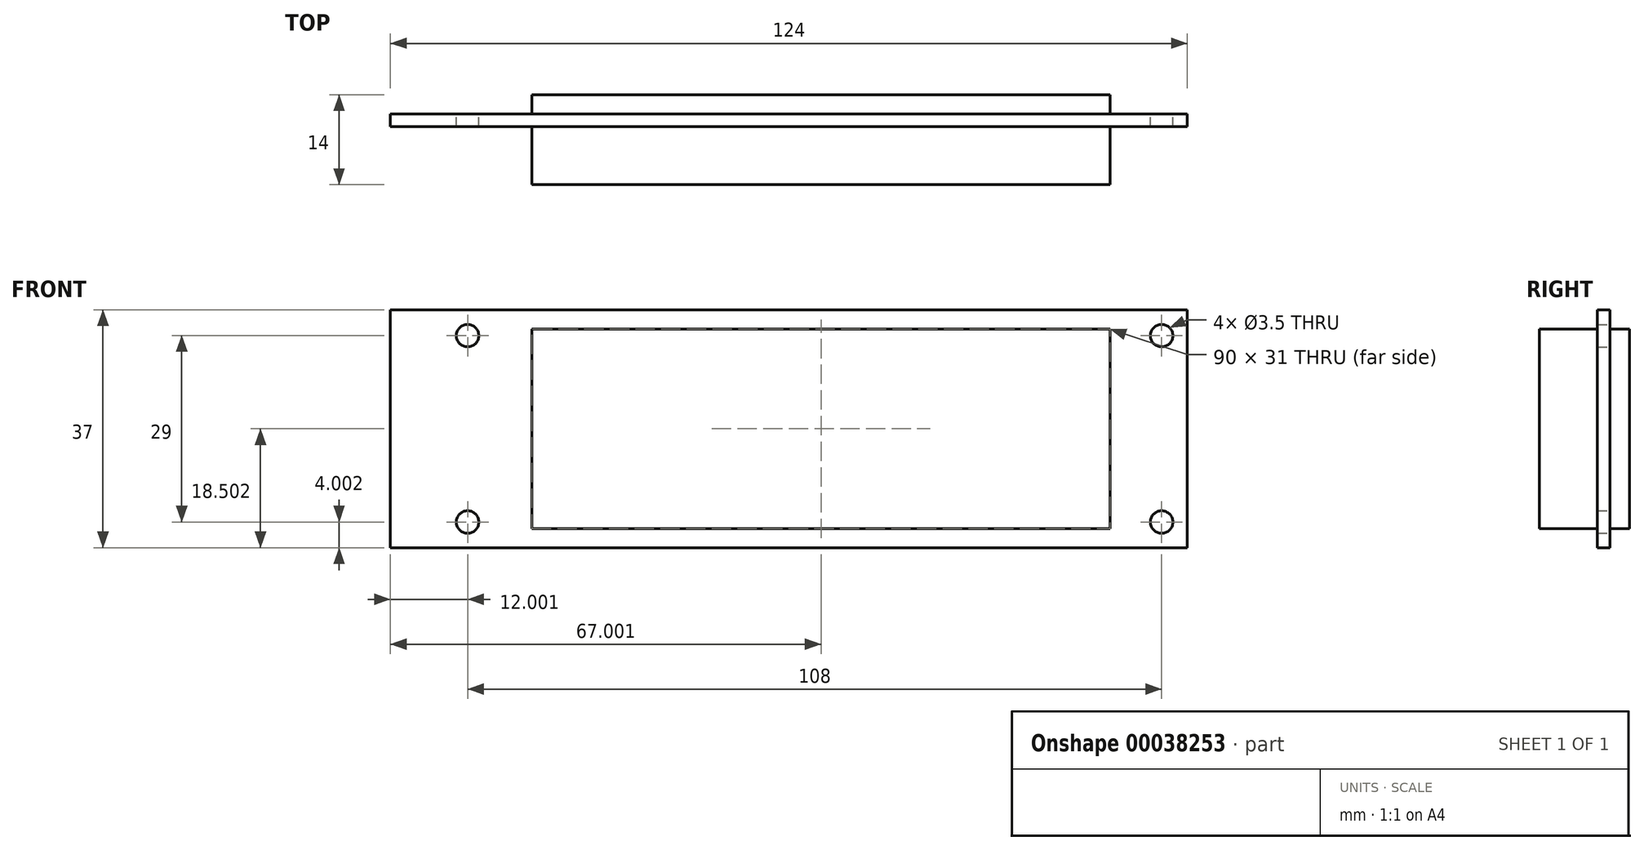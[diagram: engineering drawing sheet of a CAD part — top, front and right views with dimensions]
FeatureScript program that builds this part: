
annotation { "Feature Type Name" : "Feature", "Feature Type Description" : "" }
export const myFeature = defineFeature(function(context is Context, id is Id, definition is map)
    precondition{}
    {
        {
            var Q0;
            Q0=qCreatedBy(makeId("Front.planeOp"),FACE);
            var sketch = newSketch(context, id + "F0", { "sketchPlane" : qUnion([Q0])});
            skLineSegment(sketch, "E0.bottom", {"start": v(-121.3, -70.97) * mm, "end": v(2.7, -70.97) * mm});
            skLineSegment(sketch, "E0.top", {"start": v(-121.3, -33.97) * mm, "end": v(2.7, -33.97) * mm});
            skLineSegment(sketch, "E0.left", {"start": v(-121.3, -70.97) * mm, "end": v(-121.3, -33.97) * mm});
            skLineSegment(sketch, "E0.right", {"start": v(2.7, -70.97) * mm, "end": v(2.7, -33.97) * mm});
            skLineSegment(sketch, "E1.bottom", {"start": v(-99.3, -67.97) * mm, "end": v(-9.3, -67.97) * mm});
            skLineSegment(sketch, "E1.top", {"start": v(-99.3, -36.97) * mm, "end": v(-9.3, -36.97) * mm});
            skLineSegment(sketch, "E1.left", {"start": v(-99.3, -67.97) * mm, "end": v(-99.3, -36.97) * mm});
            skLineSegment(sketch, "E1.right", {"start": v(-9.3, -67.97) * mm, "end": v(-9.3, -36.97) * mm});
            skLineSegment(sketch, "E2", {"start": v(-109.3, -23.5) * mm, "end": v(-109.3, -79.6) * mm});
            skLineSegment(sketch, "E3", {"start": v(-131.68, -37.97) * mm, "end": v(-109.3, -37.97) * mm});
            skLineSegment(sketch, "E4", {"start": v(-135.53, -66.97) * mm, "end": v(-109.3, -66.97) * mm});
            skLineSegment(sketch, "E5", {"start": v(-1.3, -26.38) * mm, "end": v(-1.3, -82.28) * mm});
            skPoint(sketch, "E6", {"position": v(-109.3, -37.97) * mm});
            skPoint(sketch, "E7", {"position": v(-109.3, -66.97) * mm});
            skPoint(sketch, "E8", {"position": v(-1.3, -37.97) * mm});
            skPoint(sketch, "E9", {"position": v(-1.3, -66.97) * mm});
            skLineSegment(sketch, "E10.trimOffspring", {"start": v(-1.3, -37.97) * mm, "end": v(8.28, -37.97) * mm});
            skLineSegment(sketch, "E11.trimOffspring", {"start": v(-1.3, -66.97) * mm, "end": v(17.4, -66.97) * mm});
            skSolve(sketch);
        }
        {
            var Q0;
            {var subQ1=sQuery(id+"F0.wireOp",EDGE,"E4");var subQ5=sQuery(id+"F0.wireOp",EDGE,"E0.left");var subQ6=makeQuery(id+"F0.imprint","INTERSECT",VERTEX,{"derivedFrom":[subQ5,subQ1]});Q0=makeQuery(id+"F0.imprint","IMPRINT",FACE,{"disambiguationData":[TD([[makeQuery(id+"F0.imprint","IMPRINT",EDGE,{"disambiguationData":[TD([[subQ6,-1.0]])],"derivedFrom":subQ5}),-1.0]])]});}
            var Q1;
            {var subQ1=sQuery(id+"F0.wireOp",EDGE,"E0.left");var subQ5=sQuery(id+"F0.wireOp",EDGE,"E0.top");var subQ6=makeQuery(id+"F0.imprint","INTERSECT",VERTEX,{"derivedFrom":[subQ5,subQ1]});Q1=makeQuery(id+"F0.imprint","IMPRINT",FACE,{"disambiguationData":[TD([[makeQuery(id+"F0.imprint","IMPRINT",EDGE,{"disambiguationData":[TD([[subQ6,-1.0]])],"derivedFrom":subQ5}),-1.0]])]});}
            var Q2;
            Q2=makeQuery(id+"F0.imprint","IMPRINT",FACE,{"disambiguationData":[TD([[makeQuery(id+"F0.imprint","IMPRINT",EDGE,{"derivedFrom":sQuery(id+"F0.wireOp",EDGE,"E1.bottom")}),-1.0]])]});
            var Q3;
            {var subQ1=sQuery(id+"F0.wireOp",EDGE,"E0.left");var subQ5=sQuery(id+"F0.wireOp",EDGE,"E0.bottom");var subQ6=makeQuery(id+"F0.imprint","INTERSECT",VERTEX,{"derivedFrom":[subQ5,subQ1]});Q3=makeQuery(id+"F0.imprint","IMPRINT",FACE,{"disambiguationData":[TD([[makeQuery(id+"F0.imprint","IMPRINT",EDGE,{"disambiguationData":[TD([[subQ6,-1.0]])],"derivedFrom":subQ5}),1.0]])]});}
            var Q4;
            {var subQ1=sQuery(id+"F0.wireOp",EDGE,"E0.right");var subQ5=sQuery(id+"F0.wireOp",EDGE,"E0.top");var subQ6=makeQuery(id+"F0.imprint","INTERSECT",VERTEX,{"derivedFrom":[subQ5,subQ1]});Q4=makeQuery(id+"F0.imprint","IMPRINT",FACE,{"disambiguationData":[TD([[makeQuery(id+"F0.imprint","IMPRINT",EDGE,{"disambiguationData":[TD([[subQ6,1.0]])],"derivedFrom":subQ5}),-1.0]])]});}
            var Q5;
            {var subQ1=sQuery(id+"F0.wireOp",EDGE,"E11.trimOffspring");var subQ5=sQuery(id+"F0.wireOp",EDGE,"E0.right");var subQ6=makeQuery(id+"F0.imprint","INTERSECT",VERTEX,{"derivedFrom":[subQ5,subQ1]});Q5=makeQuery(id+"F0.imprint","IMPRINT",FACE,{"disambiguationData":[TD([[makeQuery(id+"F0.imprint","IMPRINT",EDGE,{"disambiguationData":[TD([[subQ6,-1.0]])],"derivedFrom":subQ5}),1.0]])]});}
            var Q6;
            {var subQ1=sQuery(id+"F0.wireOp",EDGE,"E0.right");var subQ5=sQuery(id+"F0.wireOp",EDGE,"E0.bottom");var subQ6=makeQuery(id+"F0.imprint","INTERSECT",VERTEX,{"derivedFrom":[subQ5,subQ1]});Q6=makeQuery(id+"F0.imprint","IMPRINT",FACE,{"disambiguationData":[TD([[makeQuery(id+"F0.imprint","IMPRINT",EDGE,{"disambiguationData":[TD([[subQ6,1.0]])],"derivedFrom":subQ5}),1.0]])]});}
            extrude(context, id + "F1", {"entities" : qUnion([Q0, Q1, Q2, Q3, Q4, Q5, Q6]), "depth" : 2 * mm});
        }
        {
            var Q0;
            Q0=makeQuery(id+"F0.imprint","IMPRINT",FACE,{"disambiguationData":[TD([[makeQuery(id+"F0.imprint","IMPRINT",EDGE,{"derivedFrom":sQuery(id+"F0.wireOp",EDGE,"E1.bottom")}),1.0]])]});
            extrude(context, id + "F2", {"entities" : qUnion([Q0]), "operationType" : NewBodyOperationType.ADD, "depth" : 11 * mm});
        }
        {
            var Q0;
            Q0=sQuery(id+"F0.wireOp",VERTEX,"E6");
            var Q1;
            Q1=sQuery(id+"F0.wireOp",VERTEX,"E7");
            var Q2;
            Q2=sQuery(id+"F0.wireOp",VERTEX,"E8");
            var Q3;
            Q3=sQuery(id+"F0.wireOp",VERTEX,"E9");
            var Q4;
            Q4=makeQuery(id+"F1.opExtrude","SWEPT_BODY",BODY,{"disambiguationData":[OSD([sQuery(id+"F0.wireOp",EDGE,"E0.bottom"),sQuery(id+"F0.wireOp",EDGE,"E0.top"),sQuery(id+"F0.wireOp",EDGE,"E0.left"),sQuery(id+"F0.wireOp",EDGE,"E0.right"),sQuery(id+"F0.wireOp",EDGE,"E1.bottom"),sQuery(id+"F0.wireOp",EDGE,"E1.top"),sQuery(id+"F0.wireOp",EDGE,"E1.left"),sQuery(id+"F0.wireOp",EDGE,"E1.right")])]});
            hole(context, id + "F3", {"style" : HoleStyle.SIMPLE, "holeDiameter" : 3.5 * mm, "endStyle" : HoleEndStyle.THROUGH, "oppositeDirection" : true, "locations" : qUnion([Q0, Q1, Q2, Q3]), "scope" : qUnion([Q4])});
        }
        {
            var Q0;
            Q0=makeQuery(id+"F0.imprint","IMPRINT",FACE,{"disambiguationData":[TD([[makeQuery(id+"F0.imprint","IMPRINT",EDGE,{"derivedFrom":sQuery(id+"F0.wireOp",EDGE,"E1.bottom")}),1.0]])]});
            extrude(context, id + "F4", {"entities" : qUnion([Q0]), "operationType" : NewBodyOperationType.ADD, "oppositeDirection" : true, "depth" : 3 * mm});
        }
    });
